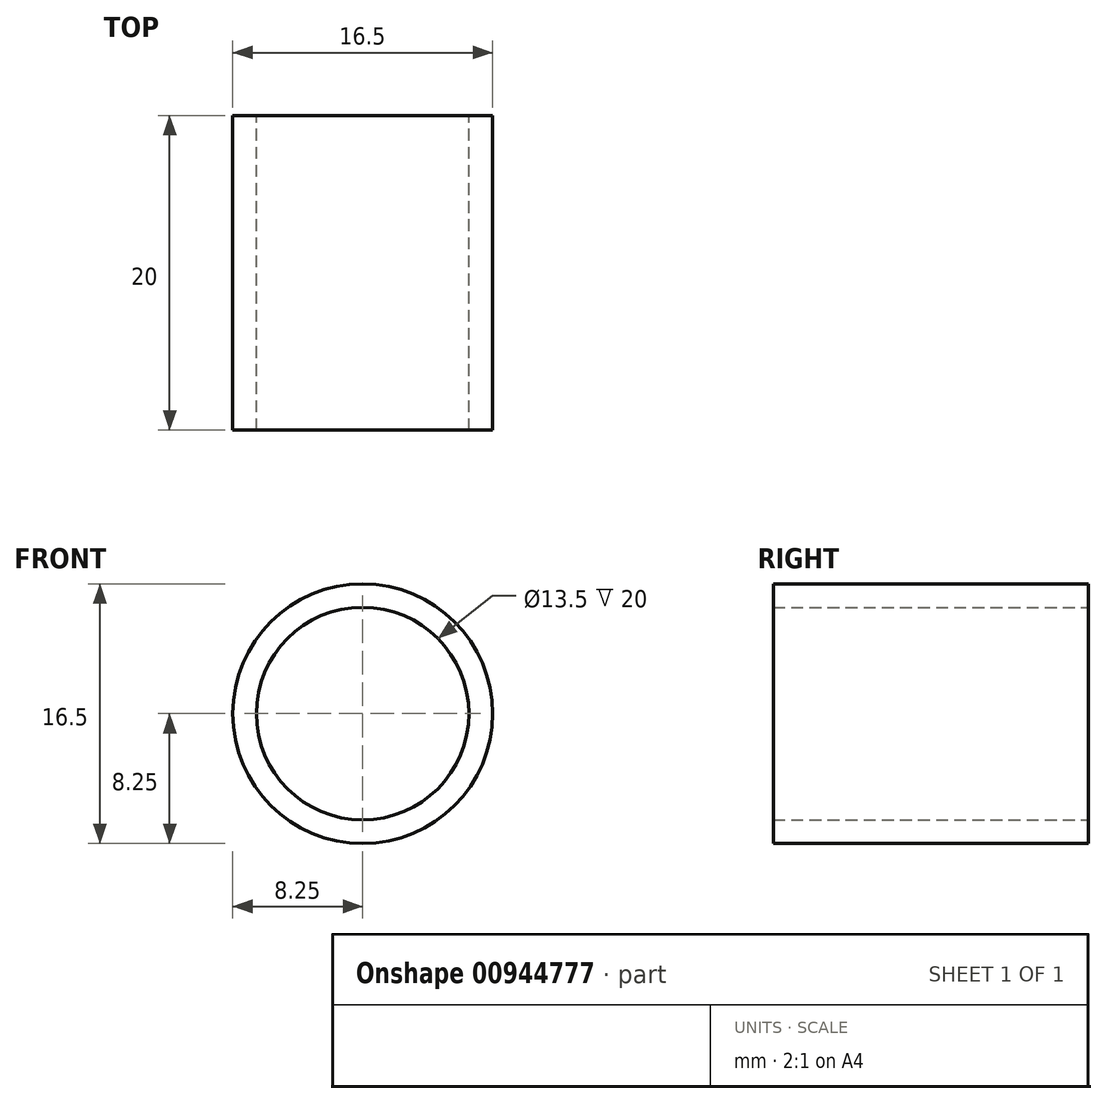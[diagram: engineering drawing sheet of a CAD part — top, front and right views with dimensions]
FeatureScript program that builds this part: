
annotation { "Feature Type Name" : "Feature", "Feature Type Description" : "" }
export const myFeature = defineFeature(function(context is Context, id is Id, definition is map)
    precondition{}
    {
        {
            var Q0;
            Q0=qCreatedBy(makeId("Front.planeOp"),FACE);
            var sketch = newSketch(context, id + "F0", { "sketchPlane" : qUnion([Q0])});
            skCircle(sketch, "E0", {"center": v(0, 0) * mm, "radius": 8.25 * mm});
            skCircle(sketch, "E1", {"center": v(0, 0) * mm, "radius": 6.75 * mm});
            skSolve(sketch);
        }
        {
            var Q0;
            Q0=makeQuery(id+"F0.imprint","IMPRINT",FACE,{"disambiguationData":[TD([[makeQuery(id+"F0.imprint","IMPRINT",EDGE,{"derivedFrom":sQuery(id+"F0.wireOp",EDGE,"E0")}),1.0]])]});
            extrude(context, id + "F1", {"entities" : qUnion([Q0]), "depth" : 20 * mm, "offsetDistance" : 25 * mm});
        }
    });
